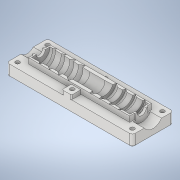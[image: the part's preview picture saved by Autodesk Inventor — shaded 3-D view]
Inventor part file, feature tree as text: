
AUTODESK INVENTOR PART (.ipt)
format: ipt  version: 2020 (Build 240168000, 168)  size: 633,344 bytes
history: native  units: mm
features: sketch x15, extrude x14, projected_geometry x9, other x4, fillet x3, boolean_combine x2, mirror x1
ambient origin geometry x8: Origin, YZ Plane, XZ Plane, XY Plane, X Axis, Y Axis, Z Axis, Center Point
bodies: Volumenkörper1 (feature_tree), Solid2 (feature_tree), Solid3 (feature_tree), Solid4 (feature_tree)
feature tree (48):
  other  "rolinho.ipt"
  extrude  "Extrusion1"  Depth=11.0mm
  other  "Spirale1"
  mirror  "Spiegeln1"
  extrude  "Extrusion5"  Depth=7.0mm
  extrude  "Extrusion6"  Depth=1.0mm
  boolean_combine  "Combine1"
  extrude  "Extrusion7"  Depth=10.0mm TaperAngle=0.0deg
  extrude  "Extrusion8"  Depth=7.0mm TaperAngle=0.0deg
  extrude  "Extrusion9"  Depth=24.0mm
  extrude  "Extrusion10"  Depth=12.0mm TaperAngle=0.0deg
  extrude  "Extrusion11"  Depth=16.0mm
  extrude  "Extrusion12"  Depth=21.0mm
  fillet  "Fillet1"  Radius=4.0mm
  extrude  "Extrusion13"  Depth=3.0mm
  fillet  "Fillet2"  Radius=3.0mm
  extrude  "Extrusion14"  Depth=4.0mm
  extrude  "Extrusion15"  Depth=4.0mm
  extrude  "Extrusion17"  Depth=4.0mm
  fillet  "Fillet3"  Radius=4.0mm
  extrude  "Extrusion18"  Depth=7.0mm
  boolean_combine  "Combine2"
  sketch  "Skizze1"  dims[d0=6.0mm d1=11.0mm]
  sketch  "Skizze3"  dims[d2=36.0mm d3=0.0mm]
  projected_geometry  "Projizierte Kontur2"
  sketch  "Sketch7"  dims[d8=7.0mm d9=24.5mm d10=10.0mm d11=0.0mm d12=90.0deg d13=90.0deg d14=0.0mm d15=0.0mm d16=4.0mm]
  sketch  "Sketch8"  dims[d17=13.962634mm d18=1.0mm]
  sketch  "Sketch9"  dims[d19=0.1mm d32=10.0mm d33=0.0mm]
  projected_geometry  "Projected Loop4"
  sketch  "Sketch10"  dims[d34=7.0mm d35=100.0mm d36=0.0mm]
  projected_geometry  "Projected Loop5"
  projected_geometry  "Projected Loop6"
  projected_geometry  "Projected Loop7"
  projected_geometry  "Projected Loop8"
  sketch  "Sketch11"  dims[d37=82.0mm d38=0.0mm d39=24.0mm]
  projected_geometry  "Projected Loop9"
  sketch  "Sketch12"  dims[d40=30.0mm d41=12.0mm d42=0.0mm]
  sketch  "Sketch13"  dims[d43=74.0mm d44=16.0mm]
  projected_geometry  "Projected Loop10"
  projected_geometry  "Projected Loop11"
  sketch  "Sketch14"  dims[d45=79.0mm d46=21.0mm d47=4.0mm d48=0.0mm]
  sketch  "Sketch15"  dims[d49=3.0mm d50=3.0mm d51=3.0mm]
  sketch  "Sketch16"  dims[d52=3.0mm d53=4.0mm]
  sketch  "Sketch17"  dims[d54=4.0mm d55=4.0mm]
  sketch  "Sketch19"  dims[d56=4.0mm d57=4.0mm d58=4.0mm]
  sketch  "Sketch20"  dims[d59=4.0mm d60=4.0mm d61=10.0mm d62=0.0mm d63=1.0mm d64=1.0mm d65=1.0mm d66=1.0mm d67=6.0mm d68=10.0mm d69=0.0mm d70=10.0mm d71=0.0mm d75=3.0mm d76=3.0mm d77=4.0mm d78=46.0mm d79=4.0mm d80=44.0mm d81=5.5mm d82=5.5mm d83=5.5mm d84=5.5mm d85=5.5mm d86=5.5mm d87=5.0mm d88=0.0mm d89=2.0mm d90=0.5mm d91=6.5mm d92=74.1mm d93=2.1mm d94=0.0mm d95=0.0mm d96=1.0mm d97=12.0mm d98=0.2mm d99=7.9mm d100=0.0mm d101=0.0mm d102=15.0mm d103=0.2mm d104=7.9mm d105=0.0mm d106=0.0mm d110=3.0mm d111=0.0mm d115=1.0mm d116=0.0mm d117=0.0mm d118=7.0mm d119=13.0mm d120=10.0mm d121=0.0mm d122=10.0mm]
  other  "Solid1::rolinho.ipt"
  other  "TaggingFeature1"
